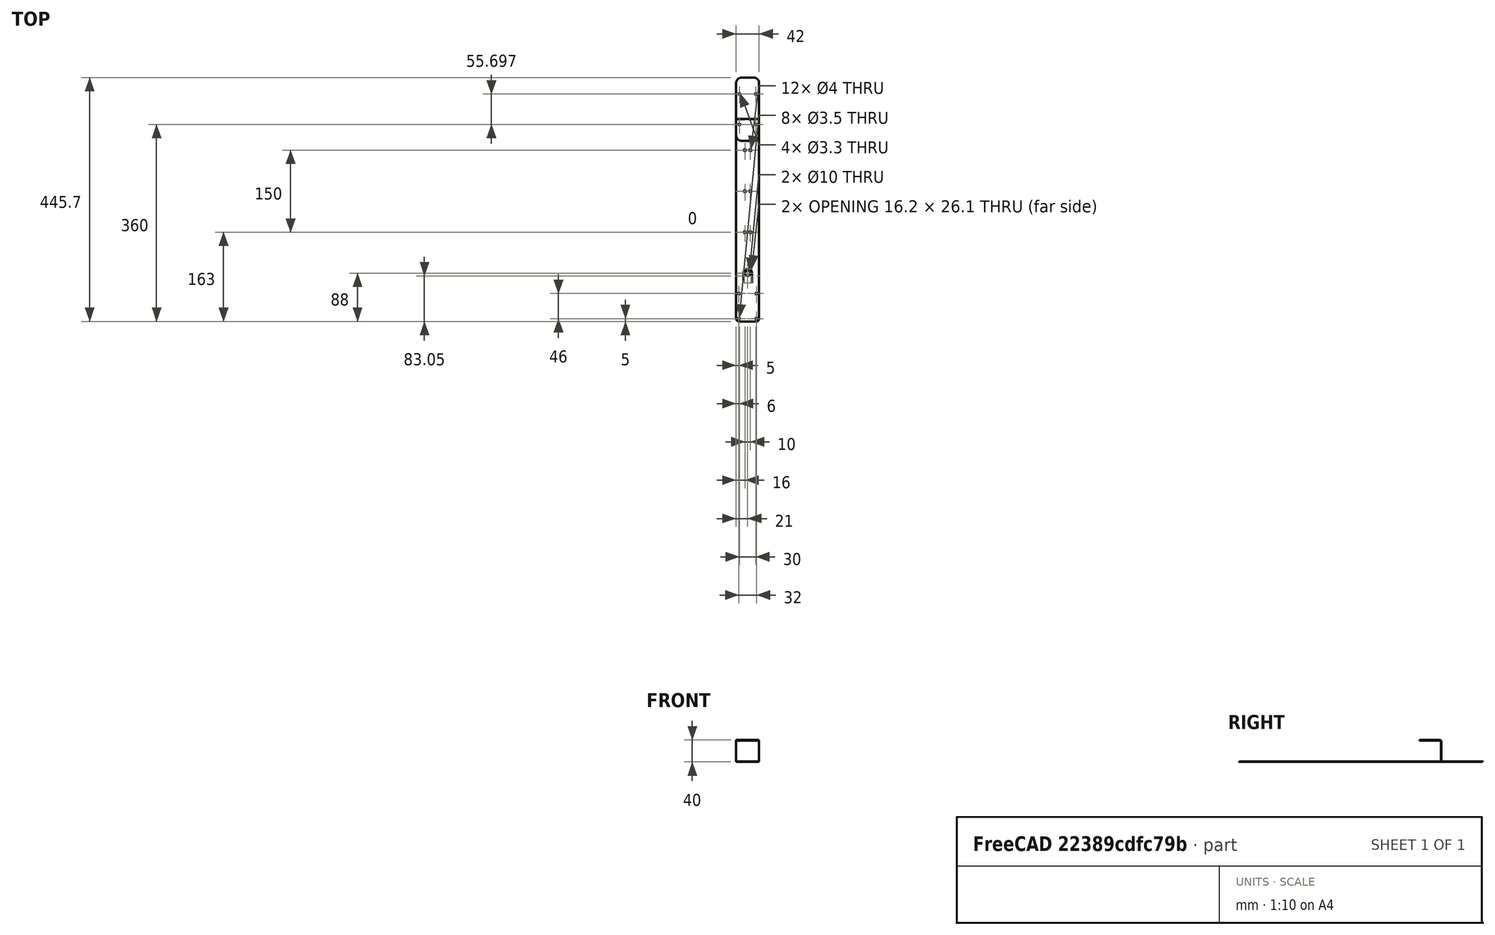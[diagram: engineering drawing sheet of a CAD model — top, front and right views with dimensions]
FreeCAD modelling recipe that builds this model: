
FCSTD DOCUMENT  (FreeCAD 0.21R32532 (Git))
Label: basin_holder
License: All rights reserved
LicenseURL: http://en.wikipedia.org/wiki/All_rights_reserved
objects: Sketcher::SketchObject×10, TechDraw::DrawViewDimension×6, PartDesign::Hole×4, PartDesign::Fillet×2, TechDraw::DrawViewPart×2, PartDesign::FeaturePython×1, Part::FeaturePython×1, Part::Compound×1, PartDesign::SubShapeBinder×1, PartDesign::CoordinateSystem×1, PartDesign::Pocket×1, PartDesign::LinearPattern×1, PartDesign::Body×1, Part::Feature×1, TechDraw::DrawSVGTemplate×1, TechDraw::DrawPage×1
note: 42 computed .brp shape members not serialized (recipe doc carries the construction recipe); baked Part::Feature solids carry a one-line shape summary decoded from their .brp

FEATURE [Sketcher::SketchObject] Sketch
  FullyConstrained = true
  MapMode = 5
  Placement = pos=(0,0,0) rot=(0.57735,0.57735,0.57735;2.0944rad)
  Support = -> [YZ_Plane]
  sketch-geometry (3):
    g0: LineSegment StartX=-185 StartY=0 StartZ=0 EndX=185 EndY=0 EndZ=0
    g1: LineSegment StartX=185 StartY=0 StartZ=0 EndX=185 EndY=40 EndZ=0
    g2: LineSegment StartX=185 StartY=40 StartZ=0 EndX=145 EndY=40 EndZ=0
  constraints (9):
    c: PointOnObject(g0,g-1)
    c: Coincident(g1,g0)
    c: Vertical(g1)
    c: Coincident(g2,g1)
    c: Horizontal(g2)
    c: DistanceY(g1,g1) = 40
    c: DistanceX(g2,g2) = 40
    c: Symmetric(g0,g0,g-2)
    c: DistanceX(g0,g0) = 370  'length'
FEATURE [PartDesign::FeaturePython] BaseBend  # WARN: FeaturePython — macro-defined, semantics opaque (R4)
  BendSide = 1
  BendSketch = -> Sketch
  MidPlane = true
  Reverse = false
  length = 42
  radius = 2
  thickness = 1
FEATURE [Sketcher::SketchObject] Sketch002
  AttachmentOffset = pos=(0,-97,0) rot=(0,0,1;0rad)
  FullyConstrained = true
  MapMode = 5
  Placement = pos=(0,-97,0) rot=(0,0,1;0rad)
  Support = -> [XY_Plane]
  expr: AttachmentOffset = Binder.Placement
  sketch-geometry (1):
    g0: Circle CenterX=0 CenterY=0 CenterZ=0 NormalX=0 NormalY=0 NormalZ=1 AngleXU=0 Radius=5
  constraints (2):
    c: Coincident(g0,g-1)
    c: Diameter(g0) = 10
FEATURE [Sketcher::SketchObject] Sketch003
  FullyConstrained = true
  sketch-geometry (5):
    g0: ArcOfCircle CenterX=0 CenterY=0 CenterZ=0 NormalX=0 NormalY=0 NormalZ=1 AngleXU=0 Radius=8 StartAngle=0 EndAngle=1.5708
    g1: ArcOfCircle CenterX=0 CenterY=0 CenterZ=0 NormalX=0 NormalY=0 NormalZ=1 AngleXU=0 Radius=8.1 StartAngle=0 EndAngle=1.5708
    g2: LineSegment StartX=8 StartY=0 StartZ=0 EndX=8 EndY=-18 EndZ=0
    g3: LineSegment StartX=8 StartY=-18 StartZ=0 EndX=8.1 EndY=-18 EndZ=0
    g4: LineSegment StartX=8.1 StartY=-18 StartZ=0 EndX=8.1 EndY=0 EndZ=0
  constraints (15):
    c: Coincident(g0,g-1)
    c: PointOnObject(g0,g-2)
    c: PointOnObject(g0,g-1)
    c: Coincident(g1,g0)
    c: PointOnObject(g1,g-2)
    c: PointOnObject(g1,g-1)
    c: Tangent(g0,g2) = 1.5708
    c: Coincident(g2,g3)
    c: Horizontal(g3)
    c: Coincident(g3,g4)
    c: Coincident(g4,g1)
    c: Vertical(g4)
    c: DistanceY(g0,g1) = 0.1
    c: Diameter(g0) = 16
    c: DistanceY(g2,g2) = 18  'length'
FEATURE [Part::FeaturePython] Mirror  label="Mirror of Sketch003"  # WARN: FeaturePython — macro-defined, semantics opaque (R4)
  ExposePlacement = false
  FlipX = true
  FlipY = false
  FlipZ = false
  MarkerShape = 1
  MarkerSize = 0
  NumElements = 0
  Object = -> Sketch003
  ObjectTraversal = 0
  Type = lattice2Mirror.LatticeMirror
  isLattice = 0
FEATURE [Part::Compound] Compound
  Links = -> [Sketch003,Mirror]
FEATURE [PartDesign::SubShapeBinder] Binder
  BindCopyOnChange = 0
  BindMode = 0
  ClaimChildren = true
  Context = -> Body [Binder.]
  Fuse = false
  MakeFace = true
  OffsetFill = false
  OffsetIntersection = false
  OffsetJoinType = 0
  OffsetOpenResult = false
  PartialLoad = false
  Placement = pos=(0,-97,0) rot=(0,0,1;0rad)
  Relative = false
  Support = -> [Compound]
  _Version = 2
  expr: .Placement.Base.y = Local_CS.Placement.Base.y + Sketch003.Constraints.length + 70 mm
FEATURE [Sketcher::SketchObject] Sketch004
  AttachmentOffset = pos=(0,75,0) rot=(0,0,1;0rad)
  FullyConstrained = true
  MapMode = 5
  Placement = pos=(0,-22,0) rot=(0,0,1;0rad)
  Support = -> [Binder]
  expr: .AttachmentOffset.Base.y = 75 mm
  expr: Support = Binder._self
  sketch-geometry (2):
    g0: Circle CenterX=5 CenterY=0 CenterZ=0 NormalX=0 NormalY=0 NormalZ=1 AngleXU=0 Radius=2
    g1: Circle CenterX=-5 CenterY=0 CenterZ=0 NormalX=0 NormalY=0 NormalZ=1 AngleXU=0 Radius=2
  constraints (5):
    c: PointOnObject(g0,g-1)
    c: Equal(g1,g0)
    c: Diameter(g1) = 4
    c: Symmetric(g1,g0,g-2)
    c: DistanceX(g1,g0) = 10
FEATURE [PartDesign::CoordinateSystem] Local_CS
  AttacherType = Attacher::AttachEngine3D
  AttachmentOffset = pos=(0,-185,0) rot=(0,0,1;0rad)
  MapMode = 5
  Placement = pos=(0,-185,0) rot=(0,0,1;0rad)
  Support = -> [XY_Plane]
  expr: .AttachmentOffset.Base.y = -Sketch.Constraints.length / 2
FEATURE [Sketcher::SketchObject] Sketch001
  AttachmentOffset = pos=(0,28,0) rot=(0,0,1;0rad)
  FullyConstrained = true
  MapMode = 5
  Placement = pos=(0,-157,0) rot=(0,0,1;0rad)
  Support = -> [Local_CS]
  expr: .AttachmentOffset.Base.y = .Constraints.y_distance / 2 + 5 mm
  expr: Support = Local_CS._self
  sketch-geometry (9):
    g0: LineSegment StartX=-16 StartY=-23 StartZ=0 EndX=-16 EndY=23 EndZ=0
    g1: LineSegment StartX=-16 StartY=23 StartZ=0 EndX=16 EndY=23 EndZ=0
    g2: LineSegment StartX=16 StartY=23 StartZ=0 EndX=16 EndY=-23 EndZ=0
    g3: LineSegment StartX=16 StartY=-23 StartZ=0 EndX=-16 EndY=-23 EndZ=0
    g4: GeomPoint X=0 Y=0 Z=0
    g5: Circle CenterX=-16 CenterY=23 CenterZ=0 NormalX=0 NormalY=0 NormalZ=1 AngleXU=0 Radius=1.75
    g6: Circle CenterX=16 CenterY=23 CenterZ=0 NormalX=0 NormalY=0 NormalZ=1 AngleXU=0 Radius=1.75
    g7: Circle CenterX=16 CenterY=-23 CenterZ=0 NormalX=0 NormalY=0 NormalZ=1 AngleXU=0 Radius=1.75
    g8: Circle CenterX=-16 CenterY=-23 CenterZ=0 NormalX=0 NormalY=0 NormalZ=1 AngleXU=0 Radius=1.75
  constraints (20):
    c: Coincident(g0,g1)
    c: Coincident(g1,g2)
    c: Coincident(g2,g3)
    c: Coincident(g3,g0)
    c: Horizontal(g1)
    c: Horizontal(g3)
    c: Vertical(g0)
    c: Vertical(g2)
    c: Symmetric(g1,g0,g4)
    c: Coincident(g4,g-1)
    c: DistanceY(g2,g2) = 46  'y_distance'
    c: DistanceX(g1,g1) = 32  'x_distance'
    c: Coincident(g5,g0)
    c: Coincident(g6,g1)
    c: Coincident(g7,g2)
    c: Coincident(g8,g0)
    c: Equal(g7,g8)
    c: Equal(g7,g5)
    c: Equal(g7,g6)
    c: Diameter(g7) = 3.5
FEATURE [Sketcher::SketchObject] Sketch005
  AttachmentOffset = pos=(0,175,2) rot=(0,0,1;0rad)
  FullyConstrained = true
  MapMode = 5
  Placement = pos=(0,175,2) rot=(0,0,1;0rad)
  Support = -> [XY_Plane]
  expr: .AttachmentOffset.Base.y = Sketch.Constraints.length / 2 - 10 mm
  expr: .AttachmentOffset.Base.z = BaseBend.thickness + 1 mm
  sketch-geometry (2):
    g0: Circle CenterX=15 CenterY=0 CenterZ=0 NormalX=0 NormalY=0 NormalZ=1 AngleXU=0 Radius=1.65
    g1: Circle CenterX=-15 CenterY=0 CenterZ=0 NormalX=0 NormalY=0 NormalZ=1 AngleXU=0 Radius=1.65
  constraints (5):
    c: PointOnObject(g0,g-1)
    c: Equal(g1,g0)
    c: Diameter(g1) = 3.3
    c: Symmetric(g0,g1,g-2)
    c: DistanceX(g1,g0) = 30
FEATURE [PartDesign::Fillet] Fillet
  Base = -> BaseBend [Edge8,Edge10]
  BaseFeature = -> BaseBend
  Radius = 10
  SupportTransform = false
  UseAllEdges = false
FEATURE [PartDesign::Fillet] Fillet001
  Base = -> Fillet [Edge48,Edge47]
  BaseFeature = -> Fillet
  Radius = 5
  SupportTransform = false
  UseAllEdges = false
FEATURE [PartDesign::Hole] Hole
  BaseFeature = -> Fillet001
  CustomThreadClearance = 0
  Depth = 756.527
  DepthType = 1
  Diameter = 3.5
  DrillForDepth = false
  DrillPoint = 1
  DrillPointAngle = 118
  HoleCutCountersinkAngle = 90
  HoleCutCustomValues = false
  HoleCutDepth = 0
  HoleCutDiameter = 6.1
  HoleCutType = 0
  ModelThread = false
  Profile = -> Sketch001
  Reversed = true
  Tapered = false
  TaperedAngle = 90
  ThreadClass = 0
  ThreadDepth = 756.527
  ThreadDepthType = 0
  ThreadDirection = 0
  ThreadFit = 0
  ThreadSize = 0
  ThreadType = 0
  Threaded = false
  UseCustomThreadClearance = false
  expr: Diameter = 3.5
FEATURE [PartDesign::Pocket] Pocket
  BaseFeature = -> Hole
  Direction = (0,0,-1)
  Length = 5
  Length2 = 5
  Profile = -> Binder
  Reversed = true
  Type = 1
FEATURE [PartDesign::Hole] Hole001
  BaseFeature = -> Pocket
  CustomThreadClearance = 0
  Depth = 25
  DepthType = 0
  Diameter = 10
  DrillForDepth = false
  DrillPoint = 1
  DrillPointAngle = 118
  HoleCutCountersinkAngle = 90
  HoleCutCustomValues = false
  HoleCutDepth = 0
  HoleCutDiameter = 6.1
  HoleCutType = 0
  ModelThread = false
  Profile = -> Sketch002
  Reversed = true
  Tapered = false
  TaperedAngle = 90
  ThreadClass = 0
  ThreadDepth = 25
  ThreadDepthType = 0
  ThreadDirection = 0
  ThreadFit = 0
  ThreadSize = 0
  ThreadType = 0
  Threaded = false
  UseCustomThreadClearance = false
FEATURE [PartDesign::Hole] Hole002
  BaseFeature = -> Hole001
  CustomThreadClearance = 0
  Depth = 25
  DepthType = 0
  Diameter = 4
  DrillForDepth = false
  DrillPoint = 1
  DrillPointAngle = 118
  HoleCutCountersinkAngle = 90
  HoleCutCustomValues = false
  HoleCutDepth = 0
  HoleCutDiameter = 6.1
  HoleCutType = 0
  ModelThread = false
  Profile = -> Sketch004
  Reversed = true
  Tapered = false
  TaperedAngle = 90
  ThreadClass = 0
  ThreadDepth = 25
  ThreadDepthType = 0
  ThreadDirection = 0
  ThreadFit = 0
  ThreadSize = 0
  ThreadType = 0
  Threaded = false
  UseCustomThreadClearance = false
FEATURE [PartDesign::LinearPattern] LinearPattern
  BaseFeature = -> Hole002
  Direction = -> Sketch004 [V_Axis]
  Length = 150
  Occurrences = 3
  Originals = -> [Hole002]
  expr: Length = 75 mm * (Occurrences - 1)
FEATURE [PartDesign::Hole] Hole003
  BaseFeature = -> LinearPattern
  CustomThreadClearance = 0
  Depth = 1070.26
  DepthType = 1
  Diameter = 3.3
  DrillForDepth = false
  DrillPoint = 1
  DrillPointAngle = 118
  HoleCutCountersinkAngle = 90
  HoleCutCustomValues = false
  HoleCutDepth = 0
  HoleCutDiameter = 6.1
  HoleCutType = 0
  ModelThread = false
  Profile = -> Sketch005
  Reversed = true
  Tapered = false
  TaperedAngle = 90
  ThreadClass = 0
  ThreadDepth = 1070.26
  ThreadDepthType = 0
  ThreadDirection = 0
  ThreadFit = 0
  ThreadSize = 0
  ThreadType = 0
  Threaded = false
  UseCustomThreadClearance = false
  expr: Diameter = 3.3
FEATURE [PartDesign::Body] Body  label="Body_material_0.45ansi"
  Group = -> [Sketch,BaseBend,Sketch001,Fillet,Fillet001,Hole,Sketch002,Binder,Pocket,Hole001,Sketch004,Hole002,LinearPattern,Local_CS,Sketch005,Hole003]
  Origin = -> Origin
  Tip = -> Hole003
FEATURE [Part::Feature] Unfold
  shape: bbox 42 x 445.7 x 1.124 mm, 31 faces (baked)
FEATURE [Sketcher::SketchObject] Unfold_Sketch
  FullyConstrained = false
  sketch-geometry (31):
    g0: LineSegment StartX=-11 StartY=260.697 StartZ=0 EndX=11 EndY=260.697 EndZ=0
    g1: BSplineCurve PolesCount=22 KnotsCount=5 Degree=6 IsPeriodic=0
    g2: BSplineCurve PolesCount=22 KnotsCount=5 Degree=6 IsPeriodic=0
    g3: LineSegment StartX=-21 StartY=-180 StartZ=0 EndX=-21 EndY=250.697 EndZ=0
    g4: BSplineCurve PolesCount=26 KnotsCount=9 Degree=4 IsPeriodic=0
    g5: LineSegment StartX=-16 StartY=-185 StartZ=0 EndX=16 EndY=-185 EndZ=0
    g6: BSplineCurve PolesCount=26 KnotsCount=9 Degree=4 IsPeriodic=0
    g7: LineSegment StartX=21 StartY=-180 StartZ=0 EndX=21 EndY=250.697 EndZ=0
    g8: ArcOfCircle CenterX=3e-16 CenterY=-97 CenterZ=0 NormalX=0 NormalY=0 NormalZ=1 AngleXU=-3.14159 Radius=8.1 StartAngle=4.71239 EndAngle=6.28319
    g9: ArcOfCircle CenterX=3e-16 CenterY=-97 CenterZ=0 NormalX=0 NormalY=0 NormalZ=1 AngleXU=0 Radius=8.1 StartAngle=0 EndAngle=1.5708
    g10: LineSegment StartX=8.1 StartY=-97 StartZ=0 EndX=8.1 EndY=-115 EndZ=0
    g11: LineSegment StartX=8.1 StartY=-115 StartZ=0 EndX=8 EndY=-115 EndZ=0
    g12: LineSegment StartX=8 StartY=-115 StartZ=0 EndX=8 EndY=-97 EndZ=0
    g13: ArcOfCircle CenterX=3e-16 CenterY=-97 CenterZ=0 NormalX=0 NormalY=0 NormalZ=1 AngleXU=0 Radius=8 StartAngle=0 EndAngle=1.5708
    g14: ArcOfCircle CenterX=3e-16 CenterY=-97 CenterZ=0 NormalX=0 NormalY=0 NormalZ=1 AngleXU=-3.14159 Radius=8 StartAngle=4.71239 EndAngle=6.28319
    g15: LineSegment StartX=-8 StartY=-115 StartZ=0 EndX=-8 EndY=-97 EndZ=0
    g16: LineSegment StartX=-8.1 StartY=-115 StartZ=0 EndX=-8 EndY=-115 EndZ=0
    g17: LineSegment StartX=-8.1 StartY=-97 StartZ=0 EndX=-8.1 EndY=-115 EndZ=0
    g18: Circle CenterX=3e-16 CenterY=-97 CenterZ=0 NormalX=0 NormalY=0 NormalZ=1 AngleXU=-3.14159 Radius=5
    g19: Circle CenterX=5 CenterY=-22 CenterZ=0 NormalX=0 NormalY=0 NormalZ=1 AngleXU=-3.14159 Radius=2
    g20: Circle CenterX=5 CenterY=53 CenterZ=0 NormalX=0 NormalY=0 NormalZ=1 AngleXU=-3.14159 Radius=2
    g21: Circle CenterX=5 CenterY=128 CenterZ=0 NormalX=0 NormalY=0 NormalZ=1 AngleXU=-3.14159 Radius=2
    g22: Circle CenterX=-5 CenterY=-22 CenterZ=0 NormalX=0 NormalY=0 NormalZ=1 AngleXU=-3.14159 Radius=2
    g23: Circle CenterX=-5 CenterY=53 CenterZ=0 NormalX=0 NormalY=0 NormalZ=1 AngleXU=-3.14159 Radius=2
    g24: Circle CenterX=-5 CenterY=128 CenterZ=0 NormalX=0 NormalY=0 NormalZ=1 AngleXU=-3.14159 Radius=2
    g25: Circle CenterX=16 CenterY=-180 CenterZ=0 NormalX=0 NormalY=0 NormalZ=1 AngleXU=-3.14159 Radius=1.75
    g26: Circle CenterX=16 CenterY=-134 CenterZ=0 NormalX=0 NormalY=0 NormalZ=1 AngleXU=-3.14159 Radius=1.75
    g27: Circle CenterX=-16 CenterY=-180 CenterZ=0 NormalX=0 NormalY=0 NormalZ=1 AngleXU=-3.14159 Radius=1.75
    g28: Circle CenterX=-16 CenterY=-134 CenterZ=0 NormalX=0 NormalY=0 NormalZ=1 AngleXU=-3.14159 Radius=1.75
    g29: Circle CenterX=15 CenterY=230.697 CenterZ=0 NormalX=0 NormalY=0 NormalZ=-1 AngleXU=4e-16 Radius=1.65
    g30: Circle CenterX=-15 CenterY=230.697 CenterZ=0 NormalX=0 NormalY=0 NormalZ=-1 AngleXU=4e-16 Radius=1.65
FEATURE [Sketcher::SketchObject] Unfold_Sketch_Outline
  FullyConstrained = false
  sketch-geometry (8):
    g0: LineSegment StartX=-11 StartY=260.697 StartZ=0 EndX=11 EndY=260.697 EndZ=0
    g1: BSplineCurve PolesCount=22 KnotsCount=5 Degree=6 IsPeriodic=0
    g2: LineSegment StartX=21 StartY=-180 StartZ=0 EndX=21 EndY=250.697 EndZ=0
    g3: BSplineCurve PolesCount=26 KnotsCount=9 Degree=4 IsPeriodic=0
    g4: LineSegment StartX=-16 StartY=-185 StartZ=0 EndX=16 EndY=-185 EndZ=0
    g5: BSplineCurve PolesCount=26 KnotsCount=9 Degree=4 IsPeriodic=0
    g6: LineSegment StartX=-21 StartY=-180 StartZ=0 EndX=-21 EndY=250.697 EndZ=0
    g7: BSplineCurve PolesCount=22 KnotsCount=5 Degree=6 IsPeriodic=0
FEATURE [Sketcher::SketchObject] Unfold_Sketch_Internal
  FullyConstrained = false
  sketch-geometry (23):
    g0: ArcOfCircle CenterX=3e-16 CenterY=-97 CenterZ=0 NormalX=0 NormalY=0 NormalZ=1 AngleXU=-3.14159 Radius=8.1 StartAngle=4.71239 EndAngle=6.28319
    g1: LineSegment StartX=-8.1 StartY=-97 StartZ=0 EndX=-8.1 EndY=-115 EndZ=0
    g2: LineSegment StartX=-8.1 StartY=-115 StartZ=0 EndX=-8 EndY=-115 EndZ=0
    g3: LineSegment StartX=-8 StartY=-115 StartZ=0 EndX=-8 EndY=-97 EndZ=0
    g4: ArcOfCircle CenterX=3e-16 CenterY=-97 CenterZ=0 NormalX=0 NormalY=0 NormalZ=1 AngleXU=-3.14159 Radius=8 StartAngle=4.71239 EndAngle=6.28319
    g5: ArcOfCircle CenterX=3e-16 CenterY=-97 CenterZ=0 NormalX=0 NormalY=0 NormalZ=1 AngleXU=0 Radius=8 StartAngle=0 EndAngle=1.5708
    g6: LineSegment StartX=8 StartY=-115 StartZ=0 EndX=8 EndY=-97 EndZ=0
    g7: LineSegment StartX=8.1 StartY=-115 StartZ=0 EndX=8 EndY=-115 EndZ=0
    g8: LineSegment StartX=8.1 StartY=-97 StartZ=0 EndX=8.1 EndY=-115 EndZ=0
    g9: ArcOfCircle CenterX=3e-16 CenterY=-97 CenterZ=0 NormalX=0 NormalY=0 NormalZ=1 AngleXU=0 Radius=8.1 StartAngle=0 EndAngle=1.5708
    g10: Circle CenterX=3e-16 CenterY=-97 CenterZ=0 NormalX=0 NormalY=0 NormalZ=1 AngleXU=-3.14159 Radius=5
    g11: Circle CenterX=-5 CenterY=128 CenterZ=0 NormalX=0 NormalY=0 NormalZ=1 AngleXU=-3.14159 Radius=2
    g12: Circle CenterX=5 CenterY=128 CenterZ=0 NormalX=0 NormalY=0 NormalZ=1 AngleXU=-3.14159 Radius=2
    g13: Circle CenterX=-5 CenterY=-22 CenterZ=0 NormalX=0 NormalY=0 NormalZ=1 AngleXU=-3.14159 Radius=2
    g14: Circle CenterX=5 CenterY=-22 CenterZ=0 NormalX=0 NormalY=0 NormalZ=1 AngleXU=-3.14159 Radius=2
    g15: Circle CenterX=-5 CenterY=53 CenterZ=0 NormalX=0 NormalY=0 NormalZ=1 AngleXU=-3.14159 Radius=2
    g16: Circle CenterX=5 CenterY=53 CenterZ=0 NormalX=0 NormalY=0 NormalZ=1 AngleXU=-3.14159 Radius=2
    g17: Circle CenterX=-16 CenterY=-134 CenterZ=0 NormalX=0 NormalY=0 NormalZ=1 AngleXU=-3.14159 Radius=1.75
    g18: Circle CenterX=-16 CenterY=-180 CenterZ=0 NormalX=0 NormalY=0 NormalZ=1 AngleXU=-3.14159 Radius=1.75
    g19: Circle CenterX=16 CenterY=-134 CenterZ=0 NormalX=0 NormalY=0 NormalZ=1 AngleXU=-3.14159 Radius=1.75
    g20: Circle CenterX=16 CenterY=-180 CenterZ=0 NormalX=0 NormalY=0 NormalZ=1 AngleXU=-3.14159 Radius=1.75
    g21: Circle CenterX=-15 CenterY=230.697 CenterZ=0 NormalX=0 NormalY=0 NormalZ=-1 AngleXU=4e-16 Radius=1.65
    g22: Circle CenterX=15 CenterY=230.697 CenterZ=0 NormalX=0 NormalY=0 NormalZ=-1 AngleXU=4e-16 Radius=1.65
FEATURE [Sketcher::SketchObject] Unfold_Sketch_bends
  FullyConstrained = false
  sketch-geometry (2):
    g0: LineSegment StartX=21 StartY=221.773 StartZ=0 EndX=-21 EndY=221.773 EndZ=0
    g1: LineSegment StartX=21 StartY=183.924 StartZ=0 EndX=-21 EndY=183.924 EndZ=0
FEATURE [TechDraw::DrawSVGTemplate] Template
  Height = 210
  Orientation = 1
  Template = <path>
  Width = 297
FEATURE [TechDraw::DrawViewPart] View
  CoarseView = false
  Direction = (1,0,0)
  Focus = 100
  HardHidden = false
  IsoCount = 0
  IsoHidden = false
  IsoVisible = false
  LockPosition = false
  Perspective = false
  Rotation = 0
  Scale = 0.7
  ScaleType = 2
  SeamHidden = false
  SeamVisible = true
  SmoothHidden = false
  SmoothVisible = true
  Source = -> [Body]
  X = 148.5
  XDirection = (0,1,-1.19209e-07)
  Y = 131
  expr: X = Template.Width / 2
FEATURE [TechDraw::DrawViewPart] View001
  CoarseView = false
  Direction = (0,0,1)
  Focus = 100
  HardHidden = false
  IsoCount = 0
  IsoHidden = false
  IsoVisible = false
  LockPosition = false
  Perspective = false
  Rotation = -90
  Scale = 0.7
  ScaleType = 2
  SeamHidden = false
  SeamVisible = true
  SmoothHidden = false
  SmoothVisible = true
  Source = -> [Body]
  X = 148.5
  XDirection = (1,0,0)
  Y = 81
  expr: X = Template.Width / 2
FEATURE [TechDraw::DrawViewDimension] Dimension
  AngleOverride = false
  Arbitrary = false
  ArbitraryTolerances = false
  EqualTolerance = true
  ExtensionAngle = 0
  FormatSpec = %.2w
  FormatSpecOverTolerance = %+.2w
  FormatSpecUnderTolerance = %+.2w
  Inverted = false
  LineAngle = 0
  LockPosition = false
  MeasureType = 1
  OverTolerance = 0
  References2D = -> [View]
  Rotation = 0
  ScaleType = 0
  TheoreticalExact = false
  Type = 2
  UnderTolerance = 0
  X = 135.696
  Y = 3.53323
FEATURE [TechDraw::DrawViewDimension] Dimension001
  AngleOverride = false
  Arbitrary = false
  ArbitraryTolerances = false
  EqualTolerance = true
  ExtensionAngle = 0
  FormatSpec = %.2w
  FormatSpecOverTolerance = %+.2w
  FormatSpecUnderTolerance = %+.2w
  Inverted = false
  LineAngle = 0
  LockPosition = false
  MeasureType = 1
  OverTolerance = 0
  References2D = -> [View]
  Rotation = 0
  ScaleType = 0
  TheoreticalExact = false
  Type = 1
  UnderTolerance = 0
  X = 117.963
  Y = 28.0373
FEATURE [TechDraw::DrawViewDimension] Dimension002
  AngleOverride = false
  Arbitrary = false
  ArbitraryTolerances = false
  EqualTolerance = true
  ExtensionAngle = 0
  FormatSpec = %.2w
  FormatSpecOverTolerance = %+.2w
  FormatSpecUnderTolerance = %+.2w
  Inverted = false
  LineAngle = 0
  LockPosition = false
  MeasureType = 1
  OverTolerance = 0
  References2D = -> [View001]
  Rotation = 0
  ScaleType = 0
  TheoreticalExact = false
  Type = 1
  UnderTolerance = 0
  X = 114.868
  Y = 23.9732
FEATURE [TechDraw::DrawViewDimension] Dimension003
  AngleOverride = false
  Arbitrary = false
  ArbitraryTolerances = false
  EqualTolerance = true
  ExtensionAngle = 0
  FormatSpec = %.2w
  FormatSpecOverTolerance = %+.2w
  FormatSpecUnderTolerance = %+.2w
  Inverted = false
  LineAngle = 0
  LockPosition = false
  MeasureType = 1
  OverTolerance = 0
  References2D = -> [View001]
  Rotation = 0
  ScaleType = 0
  TheoreticalExact = false
  Type = 1
  UnderTolerance = 0
  X = 54.4104
  Y = -29.2458
FEATURE [TechDraw::DrawViewDimension] Dimension004
  AngleOverride = false
  Arbitrary = false
  ArbitraryTolerances = false
  EqualTolerance = true
  ExtensionAngle = 0
  FormatSpec = R%.2w
  FormatSpecOverTolerance = %+.2w
  FormatSpecUnderTolerance = %+.2w
  Inverted = false
  LineAngle = 0
  LockPosition = false
  MeasureType = 1
  OverTolerance = 0
  References2D = -> [View]
  Rotation = 0
  ScaleType = 0
  TheoreticalExact = false
  Type = 4
  UnderTolerance = 0
  X = 114.043
  Y = -1.4394
FEATURE [TechDraw::DrawViewDimension] Dimension005
  AngleOverride = false
  Arbitrary = false
  ArbitraryTolerances = false
  EqualTolerance = true
  ExtensionAngle = 0
  FormatSpec = R%.2w
  FormatSpecOverTolerance = %+.2w
  FormatSpecUnderTolerance = %+.2w
  Inverted = false
  LineAngle = 0
  LockPosition = false
  MeasureType = 1
  OverTolerance = 0
  References2D = -> [View]
  Rotation = 0
  ScaleType = 0
  TheoreticalExact = false
  Type = 4
  UnderTolerance = 0
  X = 114.33
  Y = 9.47009
FEATURE [TechDraw::DrawPage] Page
  KeepUpdated = true
  NextBalloonIndex = 1
  ProjectionType = 0
  Template = -> Template
  Views = -> [View,View001,Dimension,Dimension001,Dimension002,Dimension003,Dimension004,Dimension005]
note: 1 file-system path scrubbed to <path> (originals preserved in the JSON sidecar)
